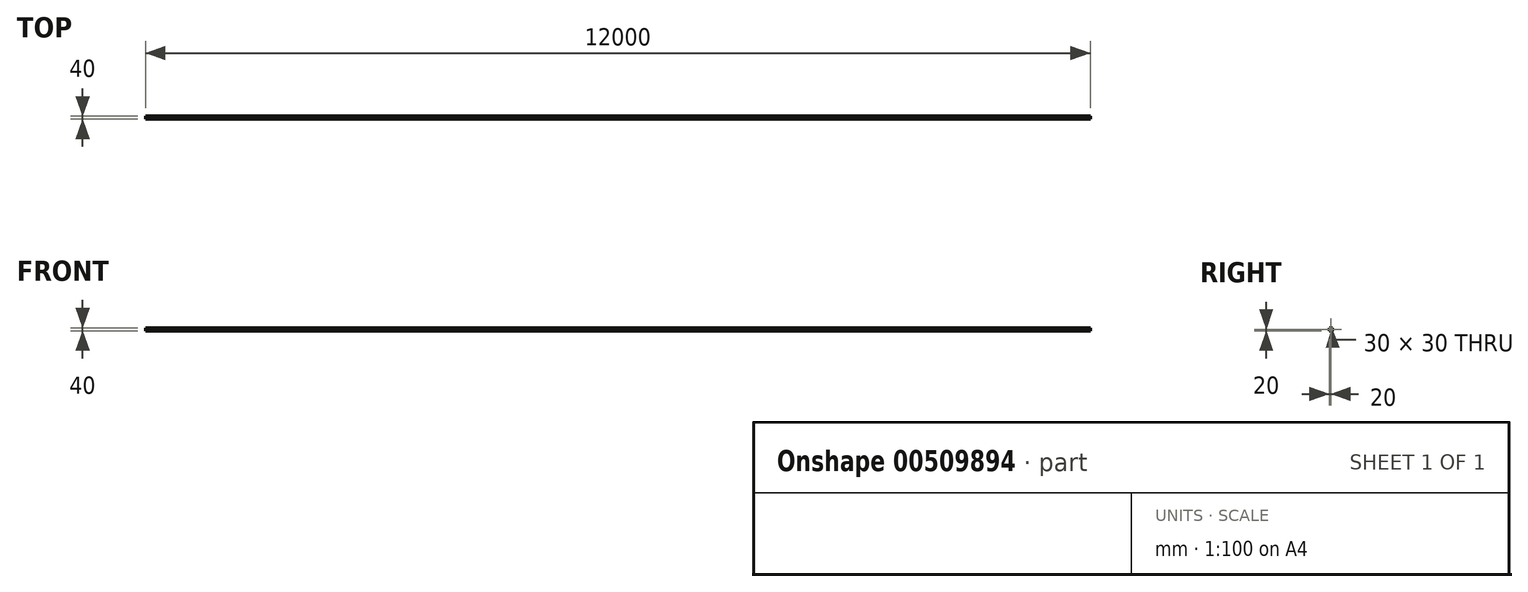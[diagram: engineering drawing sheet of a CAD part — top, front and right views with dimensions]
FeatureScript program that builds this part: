
annotation { "Feature Type Name" : "Feature", "Feature Type Description" : "" }
export const myFeature = defineFeature(function(context is Context, id is Id, definition is map)
    precondition{}
    {
        {
            var Q0;
            Q0=qCreatedBy(makeId("Right.planeOp"),FACE);
            var sketch = newSketch(context, id + "F0", { "sketchPlane" : qUnion([Q0])});
            skLineSegment(sketch, "E0.bottom", {"start": v(20, -20) * mm, "end": v(-20, -20) * mm});
            skLineSegment(sketch, "E0.top", {"start": v(20, 20) * mm, "end": v(-20, 20) * mm});
            skLineSegment(sketch, "E0.left", {"start": v(20, -20) * mm, "end": v(20, 20) * mm});
            skLineSegment(sketch, "E0.right", {"start": v(-20, -20) * mm, "end": v(-20, 20) * mm});
            skPoint(sketch, "E0.middle", {"position": v(0, 0) * mm});
            skLineSegment(sketch, "E1.bottom", {"start": v(15, -15) * mm, "end": v(-15, -15) * mm});
            skLineSegment(sketch, "E1.top", {"start": v(15, 15) * mm, "end": v(-15, 15) * mm});
            skLineSegment(sketch, "E1.left", {"start": v(15, -15) * mm, "end": v(15, 15) * mm});
            skLineSegment(sketch, "E1.right", {"start": v(-15, -15) * mm, "end": v(-15, 15) * mm});
            skSolve(sketch);
        }
        {
            var Q0;
            Q0=makeQuery(id+"F0.imprint","IMPRINT",FACE,{"disambiguationData":[TD([[makeQuery(id+"F0.imprint","IMPRINT",EDGE,{"derivedFrom":sQuery(id+"F0.wireOp",EDGE,"E0.bottom")}),-1.0]])]});
            extrude(context, id + "F1", {"entities" : qUnion([Q0]), "depth" : 12000 * mm, "offsetDistance" : 25 * mm});
        }
    });
